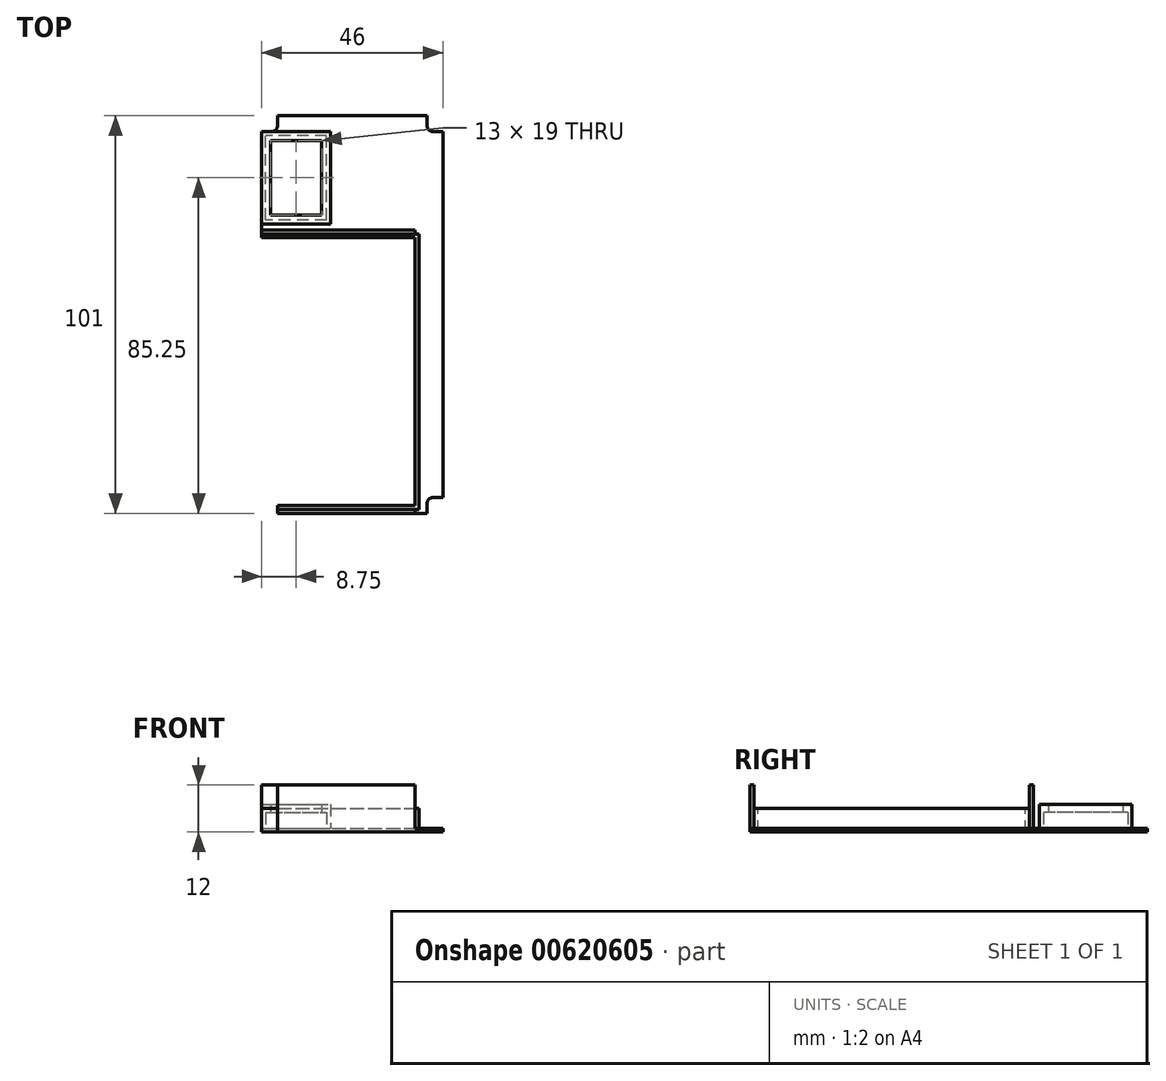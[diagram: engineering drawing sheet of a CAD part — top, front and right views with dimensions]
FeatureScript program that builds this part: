
annotation { "Feature Type Name" : "Feature", "Feature Type Description" : "" }
export const myFeature = defineFeature(function(context is Context, id is Id, definition is map)
    precondition{}
    {
        {
            assignVariable(context, id + "F0", {"name" : "Depth", "anyValue" : 30});
        }
        {
            assignVariable(context, id + "F1", {"name" : "WallThickness", "anyValue" : 2});
        }
        {
            var Q0;
            Q0=qCreatedBy(makeId("Top.planeOp"),FACE);
            var sketch = newSketch(context, id + "F2", { "sketchPlane" : qUnion([Q0])});
            skLineSegment(sketch, "E0.bottom", {"start": v(-23, 50.5) * mm, "end": v(23, 50.5) * mm});
            skLineSegment(sketch, "E0.top", {"start": v(-23, -50.5) * mm, "end": v(23, -50.5) * mm});
            skLineSegment(sketch, "E0.left", {"start": v(-23, 50.5) * mm, "end": v(-23, -50.5) * mm});
            skLineSegment(sketch, "E0.right", {"start": v(23, 50.5) * mm, "end": v(23, -50.5) * mm});
            skPoint(sketch, "E0.middle", {"position": v(0, 0) * mm});
            skSolve(sketch);
        }
        {
            var Q0;
            Q0=qSketchRegion(id+"F2",true);
            extrude(context, id + "F3", {"entities" : qUnion([Q0]), "depth" : 1 * mm, "offsetDistance" : 25 * mm});
        }
        {
            var Q0;
            Q0=makeQuery(id+"F3.opExtrude","CAP_FACE",FACE,{"disambiguationData":[OSD([sQuery(id+"F2.wireOp",EDGE,"E0.bottom"),sQuery(id+"F2.wireOp",EDGE,"E0.top"),sQuery(id+"F2.wireOp",EDGE,"E0.left"),sQuery(id+"F2.wireOp",EDGE,"E0.right")])],"isStart":false});
            var sketch = newSketch(context, id + "F4", { "sketchPlane" : qUnion([Q0])});
            skLineSegment(sketch, "E1.bottom", {"start": v(-23, 50.5) * mm, "end": v(-19, 50.5) * mm});
            skLineSegment(sketch, "E1.top", {"start": v(-23, 46.5) * mm, "end": v(-20.5, 46.5) * mm});
            skLineSegment(sketch, "E1.left", {"start": v(-23, 50.5) * mm, "end": v(-23, 46.5) * mm});
            skLineSegment(sketch, "E1.right", {"start": v(-19, 50.5) * mm, "end": v(-19, 48) * mm});
            skPoint(sketch, "E2.visualSharp", {"position": v(-19, 46.5) * mm});
            skArc(sketch, "E2.filletArc", {"start": v(-20.5, 46.5) * mm, "mid": v(-19.44, 46.94) * mm, "end": v(-19, 48) * mm});
            skPoint(sketch, "E3.MirrorP", {"position": v(19, 46.5) * mm});
            skLineSegment(sketch, "E4.MirrorCS", {"start": v(23, 50.5) * mm, "end": v(19, 50.5) * mm});
            skLineSegment(sketch, "E5.MirrorCS", {"start": v(23, 46.5) * mm, "end": v(20.5, 46.5) * mm});
            skLineSegment(sketch, "E6.MirrorCS", {"start": v(19, 50.5) * mm, "end": v(19, 48) * mm});
            skLineSegment(sketch, "E7.MirrorCS", {"start": v(23, 50.5) * mm, "end": v(23, 46.5) * mm});
            skArc(sketch, "E8.MirrorCS", {"start": v(20.5, 46.5) * mm, "mid": v(19.44, 46.94) * mm, "end": v(19, 48) * mm});
            skArc(sketch, "E9.MirrorCS", {"start": v(20.5, -46.5) * mm, "mid": v(19.44, -46.94) * mm, "end": v(19, -48) * mm});
            skArc(sketch, "E10.MirrorCS", {"start": v(-20.5, -46.5) * mm, "mid": v(-19.44, -46.94) * mm, "end": v(-19, -48) * mm});
            skLineSegment(sketch, "E11.MirrorCS", {"start": v(23, -50.5) * mm, "end": v(23, -46.5) * mm});
            skLineSegment(sketch, "E12.MirrorCS", {"start": v(19, -50.5) * mm, "end": v(19, -48) * mm});
            skPoint(sketch, "E13.MirrorP", {"position": v(19, -46.5) * mm});
            skPoint(sketch, "E14.MirrorP", {"position": v(-19, -46.5) * mm});
            skLineSegment(sketch, "E15.MirrorCS", {"start": v(-23, -50.5) * mm, "end": v(-19, -50.5) * mm});
            skLineSegment(sketch, "E16.MirrorCS", {"start": v(-23, -46.5) * mm, "end": v(-20.5, -46.5) * mm});
            skLineSegment(sketch, "E17.MirrorCS", {"start": v(-23, -50.5) * mm, "end": v(-23, -46.5) * mm});
            skLineSegment(sketch, "E18.MirrorCS", {"start": v(-19, -50.5) * mm, "end": v(-19, -48) * mm});
            skLineSegment(sketch, "E19.MirrorCS", {"start": v(23, -46.5) * mm, "end": v(20.5, -46.5) * mm});
            skLineSegment(sketch, "E20.MirrorCS", {"start": v(23, -50.5) * mm, "end": v(19, -50.5) * mm});
            skSolve(sketch);
        }
        {
            var Q0;
            Q0 = qSketchRegion(id + "F4", true);
            extrude(context, id + "F5", {"entities" : qUnion([Q0]), "operationType" : NewBodyOperationType.REMOVE, "endBound" : BoundingType.UP_TO_NEXT, "oppositeDirection" : true, "depth" : 25 * mm, "offsetDistance" : 25 * mm});
        }
        {
            var Q0;
            Q0=makeQuery(id+"F3.opExtrude","CAP_FACE",FACE,{"disambiguationData":[OSD([sQuery(id+"F2.wireOp",EDGE,"E0.bottom"),sQuery(id+"F2.wireOp",EDGE,"E0.top"),sQuery(id+"F2.wireOp",EDGE,"E0.left"),sQuery(id+"F2.wireOp",EDGE,"E0.right")])],"isStart":false});
            var sketch = newSketch(context, id + "F6", { "sketchPlane" : qUnion([Q0])});
            skLineSegment(sketch, "E21.bottom", {"start": v(-23, 19.5) * mm, "end": v(16, 19.5) * mm});
            skLineSegment(sketch, "E21.top", {"start": v(-23, -48.5) * mm, "end": v(16, -48.5) * mm});
            skLineSegment(sketch, "E21.left", {"start": v(-23, 19.5) * mm, "end": v(-23, -48.5) * mm});
            skLineSegment(sketch, "E21.right", {"start": v(16, 19.5) * mm, "end": v(16, -48.5) * mm});
            skSolve(sketch);
        }
        {
            var Q0;
            Q0 = qSketchRegion(id + "F6", true);
            extrude(context, id + "F7", {"entities" : qUnion([Q0]), "operationType" : NewBodyOperationType.REMOVE, "endBound" : BoundingType.UP_TO_NEXT, "oppositeDirection" : true, "depth" : 25 * mm, "offsetDistance" : 25 * mm});
        }
        {
            var Q0;
            Q0=makeQuery(id+"F3.opExtrude","CAP_FACE",FACE,{"disambiguationData":[OSD([sQuery(id+"F2.wireOp",EDGE,"E0.bottom"),sQuery(id+"F2.wireOp",EDGE,"E0.top"),sQuery(id+"F2.wireOp",EDGE,"E0.left"),sQuery(id+"F2.wireOp",EDGE,"E0.right")])],"isStart":false});
            var sketch = newSketch(context, id + "F8", { "sketchPlane" : qUnion([Q0])});
            skLineSegment(sketch, "E22.bottom", {"start": v(-23, 21.5) * mm, "end": v(16, 21.5) * mm});
            skLineSegment(sketch, "E22.top", {"start": v(-23, 20.5) * mm, "end": v(16, 20.5) * mm});
            skLineSegment(sketch, "E22.left", {"start": v(-23, 21.5) * mm, "end": v(-23, 20.5) * mm});
            skLineSegment(sketch, "E22.right", {"start": v(16, 21.5) * mm, "end": v(16, 20.5) * mm});
            skLineSegment(sketch, "E23.bottom", {"start": v(-19, -50.5) * mm, "end": v(16, -50.5) * mm});
            skLineSegment(sketch, "E23.top", {"start": v(-19, -49.5) * mm, "end": v(16, -49.5) * mm});
            skLineSegment(sketch, "E23.left", {"start": v(-19, -50.5) * mm, "end": v(-19, -49.5) * mm});
            skLineSegment(sketch, "E23.right", {"start": v(16, -50.5) * mm, "end": v(16, -49.5) * mm});
            skSolve(sketch);
        }
        {
            var Q0;
            Q0 = qSketchRegion(id + "F8", true);
            extrude(context, id + "F9", {"entities" : qUnion([Q0]), "operationType" : NewBodyOperationType.ADD, "depth" : (getVariable(context, 'Depth') - 2 * getVariable(context, 'WallThickness') - 15) * mm, "offsetDistance" : 25 * mm});
        }
        {
            var Q0;
            Q0=makeQuery(id+"F3.opExtrude","CAP_FACE",FACE,{"disambiguationData":[OSD([sQuery(id+"F2.wireOp",EDGE,"E0.bottom"),sQuery(id+"F2.wireOp",EDGE,"E0.top"),sQuery(id+"F2.wireOp",EDGE,"E0.left"),sQuery(id+"F2.wireOp",EDGE,"E0.right")])],"isStart":false});
            var sketch = newSketch(context, id + "F10", { "sketchPlane" : qUnion([Q0])});
            skLineSegment(sketch, "E24.bottom", {"start": v(-23, 19.5) * mm, "end": v(17, 19.5) * mm});
            skLineSegment(sketch, "E24.top", {"start": v(-23, 20.5) * mm, "end": v(17, 20.5) * mm});
            skLineSegment(sketch, "E24.left", {"start": v(-23, 19.5) * mm, "end": v(-23, 20.5) * mm});
            skLineSegment(sketch, "E24.right", {"start": v(17, 19.5) * mm, "end": v(17, 20.5) * mm});
            skLineSegment(sketch, "E25.bottom", {"start": v(-19, -49.5) * mm, "end": v(17, -49.5) * mm});
            skLineSegment(sketch, "E25.top", {"start": v(-19, -48.5) * mm, "end": v(17, -48.5) * mm});
            skLineSegment(sketch, "E25.left", {"start": v(-19, -49.5) * mm, "end": v(-19, -48.5) * mm});
            skLineSegment(sketch, "E25.right", {"start": v(17, -49.5) * mm, "end": v(17, -48.5) * mm});
            skLineSegment(sketch, "E26.bottom", {"start": v(16, 19.5) * mm, "end": v(17, 19.5) * mm});
            skLineSegment(sketch, "E26.top", {"start": v(16, -48.5) * mm, "end": v(17, -48.5) * mm});
            skLineSegment(sketch, "E26.left", {"start": v(16, 19.5) * mm, "end": v(16, -48.5) * mm});
            skLineSegment(sketch, "E26.right", {"start": v(17, 19.5) * mm, "end": v(17, -48.5) * mm});
            skSolve(sketch);
        }
        {
            var Q0;
            Q0 = qSketchRegion(id + "F10", true);
            extrude(context, id + "F11", {"entities" : qUnion([Q0]), "operationType" : NewBodyOperationType.ADD, "depth" : 5 * mm, "offsetDistance" : 25 * mm});
        }
        {
            var Q0;
            Q0=makeQuery(id+"F3.opExtrude","CAP_FACE",FACE,{"disambiguationData":[OSD([sQuery(id+"F2.wireOp",EDGE,"E0.bottom"),sQuery(id+"F2.wireOp",EDGE,"E0.top"),sQuery(id+"F2.wireOp",EDGE,"E0.left"),sQuery(id+"F2.wireOp",EDGE,"E0.right")])],"isStart":false});
            var sketch = newSketch(context, id + "F12", { "sketchPlane" : qUnion([Q0])});
            skLineSegment(sketch, "E27.bottom", {"start": v(-23, 46.5) * mm, "end": v(-5.5, 46.5) * mm});
            skLineSegment(sketch, "E27.top", {"start": v(-23, 23) * mm, "end": v(-5.5, 23) * mm});
            skLineSegment(sketch, "E27.left", {"start": v(-23, 46.5) * mm, "end": v(-23, 23) * mm});
            skLineSegment(sketch, "E27.right", {"start": v(-5.5, 46.5) * mm, "end": v(-5.5, 23) * mm});
            skPoint(sketch, "E27.middle", {"position": v(-14.25, 34.75) * mm});
            skLineSegment(sketch, "E28.bottom", {"start": v(-22, 45.5) * mm, "end": v(-6.5, 45.5) * mm});
            skLineSegment(sketch, "E28.top", {"start": v(-22, 24) * mm, "end": v(-6.5, 24) * mm});
            skLineSegment(sketch, "E28.left", {"start": v(-22, 45.5) * mm, "end": v(-22, 24) * mm});
            skLineSegment(sketch, "E28.right", {"start": v(-6.5, 45.5) * mm, "end": v(-6.5, 24) * mm});
            skSolve(sketch);
        }
        {
            var Q0;
            Q0 = qSketchRegion(id + "F12", true);
            extrude(context, id + "F13", {"entities" : qUnion([Q0]), "operationType" : NewBodyOperationType.ADD, "depth" : 4 * mm, "offsetDistance" : 25 * mm});
        }
        {
            var Q0;
            Q0=makeQuery(id+"F13.boolean.opBoolean","SPLIT",FACE,{"disambiguationData":[TD([makeQuery(id+"F13.opExtrude","SWEPT_FACE",FACE,{"disambiguationData":[OSD([sQuery(id+"F12.wireOp",EDGE,"E28.bottom")])]})])],"derivedFrom":makeQuery(id+"F3.opExtrude","CAP_FACE",FACE,{"disambiguationData":[OSD([sQuery(id+"F2.wireOp",EDGE,"E0.bottom"),sQuery(id+"F2.wireOp",EDGE,"E0.top"),sQuery(id+"F2.wireOp",EDGE,"E0.left"),sQuery(id+"F2.wireOp",EDGE,"E0.right")])],"isStart":false})});
            var sketch = newSketch(context, id + "F14", { "sketchPlane" : qUnion([Q0])});
            skLineSegment(sketch, "E29.bottom", {"start": v(-22, 45.5) * mm, "end": v(-6.5, 45.5) * mm});
            skLineSegment(sketch, "E29.top", {"start": v(-22, 24) * mm, "end": v(-6.5, 24) * mm});
            skLineSegment(sketch, "E29.left", {"start": v(-22, 45.5) * mm, "end": v(-22, 24) * mm});
            skLineSegment(sketch, "E29.right", {"start": v(-6.5, 45.5) * mm, "end": v(-6.5, 24) * mm});
            skSolve(sketch);
        }
        {
            var Q0;
            Q0 = qSketchRegion(id + "F14", true);
            extrude(context, id + "F15", {"entities" : qUnion([Q0]), "operationType" : NewBodyOperationType.REMOVE, "endBound" : BoundingType.UP_TO_NEXT, "oppositeDirection" : true, "depth" : 25 * mm, "offsetDistance" : 25 * mm});
        }
        {
            var Q0;
            Q0=makeQuery(id+"F13.opExtrude","CAP_FACE",FACE,{"disambiguationData":[OSD([sQuery(id+"F12.wireOp",EDGE,"E27.bottom"),sQuery(id+"F12.wireOp",EDGE,"E27.top"),sQuery(id+"F12.wireOp",EDGE,"E27.left"),sQuery(id+"F12.wireOp",EDGE,"E27.right"),sQuery(id+"F12.wireOp",EDGE,"E28.bottom"),sQuery(id+"F12.wireOp",EDGE,"E28.top"),sQuery(id+"F12.wireOp",EDGE,"E28.left"),sQuery(id+"F12.wireOp",EDGE,"E28.right")])],"isStart":false});
            var sketch = newSketch(context, id + "F16", { "sketchPlane" : qUnion([Q0])});
            skLineSegment(sketch, "E30.bottom", {"start": v(-23, 46.5) * mm, "end": v(-5.5, 46.5) * mm});
            skLineSegment(sketch, "E30.top", {"start": v(-23, 23) * mm, "end": v(-5.5, 23) * mm});
            skLineSegment(sketch, "E30.left", {"start": v(-23, 46.5) * mm, "end": v(-23, 23) * mm});
            skLineSegment(sketch, "E30.right", {"start": v(-5.5, 46.5) * mm, "end": v(-5.5, 23) * mm});
            skPoint(sketch, "E30.middle", {"position": v(-14.25, 34.75) * mm});
            skLineSegment(sketch, "E31.bottom", {"start": v(-20.75, 44.25) * mm, "end": v(-7.75, 44.25) * mm});
            skLineSegment(sketch, "E31.top", {"start": v(-20.75, 25.25) * mm, "end": v(-7.75, 25.25) * mm});
            skLineSegment(sketch, "E31.left", {"start": v(-20.75, 44.25) * mm, "end": v(-20.75, 25.25) * mm});
            skLineSegment(sketch, "E31.right", {"start": v(-7.75, 44.25) * mm, "end": v(-7.75, 25.25) * mm});
            skSolve(sketch);
        }
        {
            var Q0;
            Q0 = qSketchRegion(id + "F16", true);
            extrude(context, id + "F17", {"entities" : qUnion([Q0]), "operationType" : NewBodyOperationType.ADD, "depth" : 2 * mm, "offsetDistance" : 25 * mm});
        }
    });
